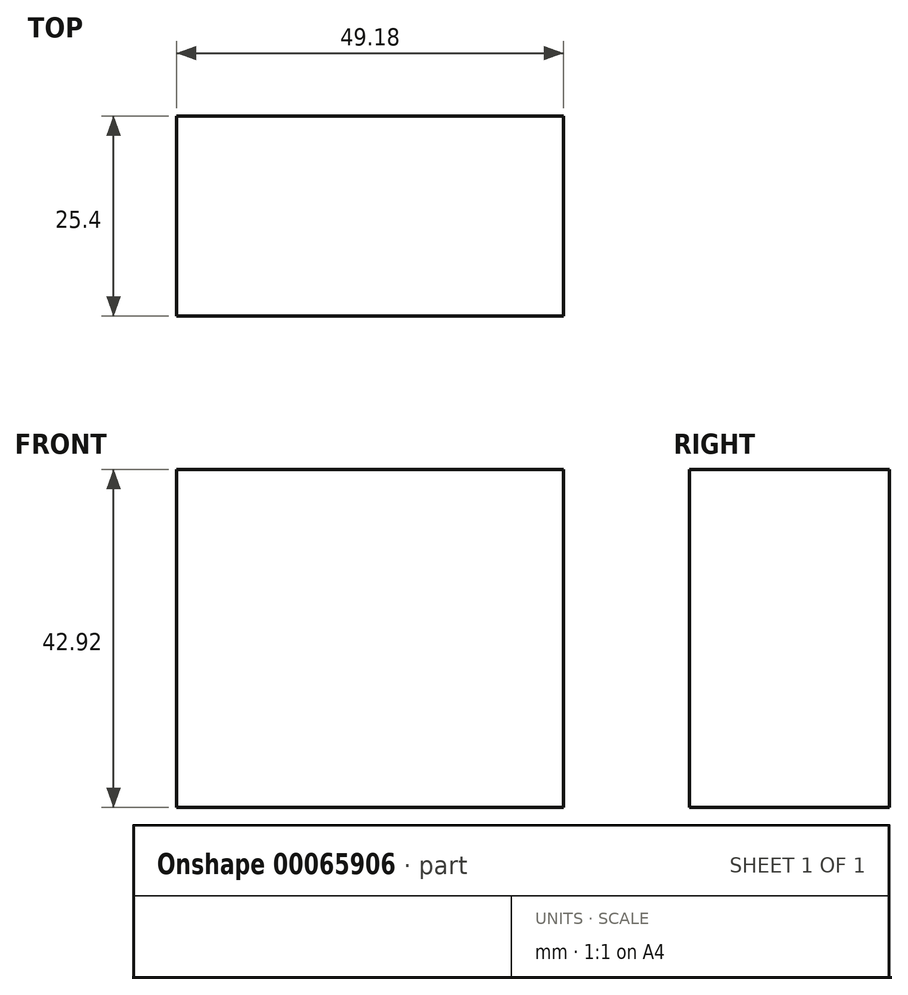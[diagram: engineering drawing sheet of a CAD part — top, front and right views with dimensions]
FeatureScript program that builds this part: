
annotation { "Feature Type Name" : "Feature", "Feature Type Description" : "" }
export const myFeature = defineFeature(function(context is Context, id is Id, definition is map)
    precondition{}
    {
        {
            var Q0;
            Q0=qCreatedBy(makeId("Front.planeOp"),FACE);
            var sketch = newSketch(context, id + "F0", { "sketchPlane" : qUnion([Q0])});
            skLineSegment(sketch, "E0", {"start": v(0, 0) * mm, "end": v(0, 42.92) * mm});
            skLineSegment(sketch, "E1", {"start": v(0, 42.92) * mm, "end": v(49.18, 42.92) * mm});
            skLineSegment(sketch, "E2", {"start": v(49.18, 42.92) * mm, "end": v(49.18, 0) * mm});
            skLineSegment(sketch, "E3", {"start": v(49.18, 0) * mm, "end": v(0, 0) * mm});
            skSolve(sketch);
        }
        {
            var Q0;
            Q0 = qSketchRegion(id + "F0", true);
            extrude(context, id + "F1", {"entities" : qUnion([Q0]), "depth" : 25.4 * mm});
        }
    });
